# Revit family: 353_Gutter drainage SVK 400_160
name_source: partatom
category: Plumbing Fixtures
units: mm (PartAtom-declared; Revit-internal decimal feet)

## family parameters
Always vertical = Yes
Cut with Voids When Loaded = No
Part Type = Normal
Room Calculation Point = No
Round Connector Dimension = Use Diameter
Shared = No
Work Plane-Based = No

## types (1)
- Gutter drain chamber kit p/n 086356-160
    BD = 698 mm  [stored 2.29003 ft]
    CAT0 = Yes
    CLBTZ = 0 mm  [stored 0 ft]
    CL_Location_5000 = 5000 mm  [stored 16.4042 ft]
    CX1 = 397 mm
    CX11 = 278 mm
    CX11__ve = -278 mm
    CX2 = 176 mm
    CX2__ve = -176 mm
    CX3 = 80 mm  [stored 0.262467 ft]
    CX3__ve = -80 mm  [stored -0.262467 ft]
    D = 160 mm
    D11 = No
    D16 = Yes
    D20 = No
    DC1 = Yes
    DC2 = No
    DT1 = 530 mm
    DT2 = 398 mm
    Description = Gutter drain chamber kit p/n:086356
    H = 380 mm  [stored 1.24672 ft]
    MC Product Code = Gutter drain chamber kit p/n:086356-160
    Manufacturer = Pipelife
    QmdConnectorList = 651;D
    R = 80 mm  [stored 0.262467 ft]
    URL = http://www.pipelife.fi
    ZT = 13 mm
    ZT__ve = -13 mm
    magiPartTypeId = 353
    magiProductFamilyId = Gutter drainage SVK 400/160
    magiProductId = Gutter drainage SVK 400/160

note: [stored X ft] marks values corroborated as IEEE doubles in the binary element streams (Revit-internal decimal feet)

## geometry (parser evidence)
native form markers: Sweep x2
no freeform markers — native parametric forms only
